# Revit family: LED RECESSED CEILING MOUNT EMERGENCY LIGHT
name_source: partatom
category: Lighting Fixtures
units: mm (PartAtom-declared; Revit-internal decimal feet)

## family parameters
Always vertical = No
Cut with Voids When Loaded = No
Light Source = Yes
Part Type = Normal
Room Calculation Point = No
Round Connector Dimension = Use Radius
Shared = No
Work Plane-Based = No

## types (1)
- STD
    Apparent Load = 0 VA
    Application = Emergency Lighting
    Application Environment = Indoor
    Color Filter = 16777215
    Dimming Lamp Color Temperature Shift = <None>
    Emergency = Yes
    Emergency Light Fixture Tag = E6
    Emit from Line Length = 85 mm  [stored 0.278871 ft]
    IP Rating = IP20
    L2D = 85 mm  [stored 0.278871 ft]
    Lamp = 4 x 1W LED
    Luminaire Type = LED
    Mounting Type = Ceiling Recessed
    Number of Poles = 1
    Photometric Web File = SN_9104_4x1W.ies
    Real Power = 8 W
    Tilt Angle = 60.00°
    Voltage = 230 V
    W2D = 85 mm  [stored 0.278871 ft]

note: [stored X ft] marks values corroborated as IEEE doubles in the binary element streams (Revit-internal decimal feet)

## geometry (parser evidence)
native form markers: Sweep x7
no freeform markers — native parametric forms only
